# Revit family: QF_OSCARTEK_LA_CROSSE_N1150_cat
name_source: partatom
category: Specialty Equipment
units: mm (PartAtom-declared; Revit-internal decimal feet)

## family parameters
Always vertical = Yes
Cut with Voids When Loaded = No
Enable Cutting in Views = No
Maintain Annotation Orientation = No
Part Type = Normal
Room Calculation Point = No
Round Connector Dimension = Use Diameter
Shared = No
Work Plane-Based = No

## types (1)
- QF_OSCARTEK_LA_CROSSE_N1150_cat
    Apparent Power = 0 VA
    Conn Conduit = Yes
    Cycle = 60 Hz
    Default Elevation = 0"
    Depth = 45 3/8"
    Description = NEUTRAL SHOWCASE
    Elec Conn Connection Height = 0"
    Elec Conn RI Height = 0"
    FL Amps = 2 A
    Foodservice Equipment Identifier = Yes
    Height = 45 1/4"
    Identify Quantity as Lot = Yes
    Length = 47 5/8"
    Manufacturer = OSCARTEK
    Max Overcurrent Protection = 0 A
    Min Ckt Ampacity = 0 A
    Model = LA CROSSE PN1150
    Number of Poles = 1
    Phase = 1
    Volts = 208 V
    Watts = 416 W
    Weight in Pounds = 385

## geometry (parser evidence)
native form markers: Blend x16, Sweep x2
no freeform markers — native parametric forms only
